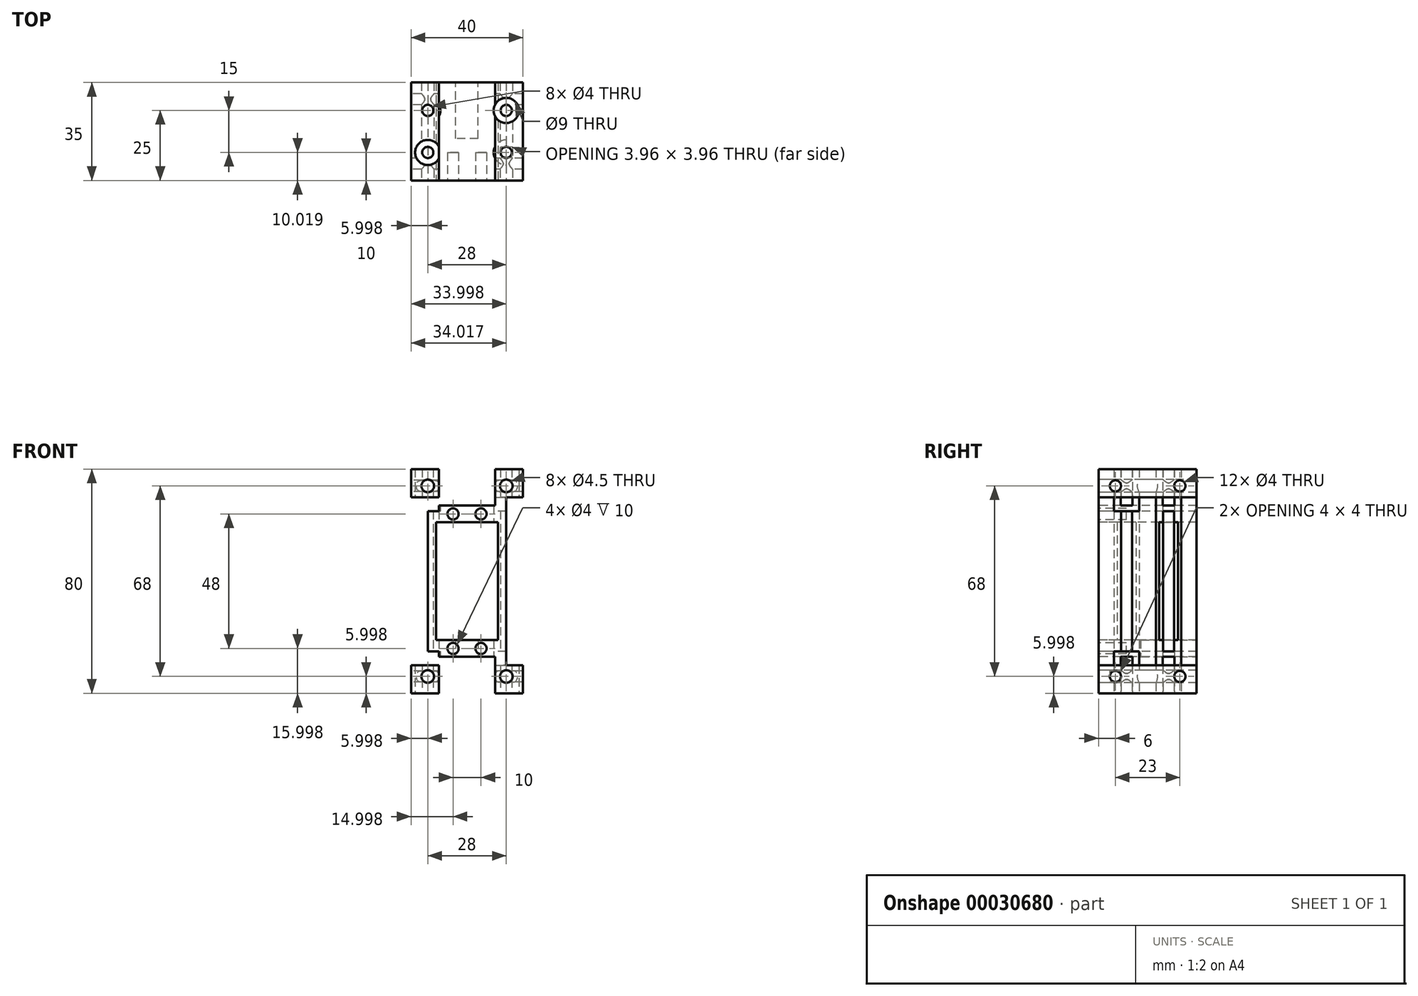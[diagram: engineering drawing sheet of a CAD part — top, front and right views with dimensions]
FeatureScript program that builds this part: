
annotation { "Feature Type Name" : "Feature", "Feature Type Description" : "" }
export const myFeature = defineFeature(function(context is Context, id is Id, definition is map)
    precondition{}
    {
        {
            var Q0;
            Q0=qCreatedBy(makeId("Front.planeOp"),FACE);
            var sketch = newSketch(context, id + "F0", { "sketchPlane" : qUnion([Q0])});
            skLineSegment(sketch, "E0.bottom", {"start": v(-33.97, 64.46) * mm, "end": v(6.03, 64.46) * mm});
            skLineSegment(sketch, "E0.top", {"start": v(-33.97, -15.54) * mm, "end": v(6.03, -15.54) * mm});
            skLineSegment(sketch, "E0.left", {"start": v(-33.97, 64.46) * mm, "end": v(-33.97, -15.54) * mm});
            skLineSegment(sketch, "E0.right", {"start": v(6.03, 64.46) * mm, "end": v(6.03, -15.54) * mm});
            skSolve(sketch);
        }
        {
            var Q0;
            Q0 = qSketchRegion(id + "F0", true);
            var Q1;
            Q1=makeQuery(id+"F0.imprint","IMPRINT",FACE,{"disambiguationData":[TD([[makeQuery(id+"F0.imprint","IMPRINT",EDGE,{"derivedFrom":sQuery(id+"F0.wireOp",EDGE,"E0.bottom")}),-1.0]])]});
            extrude(context, id + "F1", {"entities" : qUnion([Q0, Q1]), "depth" : 35 * mm});
        }
        {
            var Q0;
            Q0=makeQuery(id+"F1.opExtrude","CAP_FACE",FACE,{"disambiguationData":[OSD([sQuery(id+"F0.wireOp",EDGE,"E0.bottom"),sQuery(id+"F0.wireOp",EDGE,"E0.top"),sQuery(id+"F0.wireOp",EDGE,"E0.left"),sQuery(id+"F0.wireOp",EDGE,"E0.right")])],"isStart":false});
            var sketch = newSketch(context, id + "F2", { "sketchPlane" : qUnion([Q0])});
            skLineSegment(sketch, "E1.bottom", {"start": v(-24.97, 45.46) * mm, "end": v(-2.97, 45.46) * mm});
            skLineSegment(sketch, "E1.top", {"start": v(-24.97, 3.46) * mm, "end": v(-2.97, 3.46) * mm});
            skLineSegment(sketch, "E1.left", {"start": v(-24.97, 45.46) * mm, "end": v(-24.97, 3.46) * mm});
            skLineSegment(sketch, "E1.right", {"start": v(-2.97, 45.46) * mm, "end": v(-2.97, 3.46) * mm});
            skLineSegment(sketch, "E2", {"start": v(-13.97, 3.46) * mm, "end": v(-13.97, 13.46) * mm, "construction": true});
            skLineSegment(sketch, "E3.bottom", {"start": v(6.03, 54.46) * mm, "end": v(0.03, 54.46) * mm});
            skLineSegment(sketch, "E3.top", {"start": v(6.03, -5.54) * mm, "end": v(0.03, -5.54) * mm});
            skLineSegment(sketch, "E3.left", {"start": v(6.03, 54.46) * mm, "end": v(6.03, -5.54) * mm});
            skLineSegment(sketch, "E3.right", {"start": v(0.03, 54.46) * mm, "end": v(0.03, -5.54) * mm});
            skLineSegment(sketch, "E4", {"start": v(6.03, -5.54) * mm, "end": v(6.03, -15.54) * mm, "construction": true});
            skLineSegment(sketch, "E5", {"start": v(6.03, 54.46) * mm, "end": v(6.03, 64.46) * mm, "construction": true});
            skLineSegment(sketch, "E6.MirrorCS", {"start": v(-27.97, 54.46) * mm, "end": v(-27.97, -5.54) * mm});
            skLineSegment(sketch, "E7.MirrorCS", {"start": v(-33.97, 54.46) * mm, "end": v(-27.97, 54.46) * mm});
            skLineSegment(sketch, "E8.MirrorCS", {"start": v(-33.97, 54.46) * mm, "end": v(-33.97, -5.54) * mm});
            skLineSegment(sketch, "E9.MirrorCS", {"start": v(-33.97, -5.54) * mm, "end": v(-27.97, -5.54) * mm});
            skPoint(sketch, "E10", {"position": v(-33.97, 24.46) * mm});
            skLineSegment(sketch, "E11", {"start": v(-33.97, 24.46) * mm, "end": v(6.03, 24.46) * mm, "construction": true});
            skLineSegment(sketch, "E12.bottom", {"start": v(-3.97, -15.54) * mm, "end": v(-23.97, -15.54) * mm});
            skLineSegment(sketch, "E12.top", {"start": v(-3.97, -2.54) * mm, "end": v(-23.97, -2.54) * mm});
            skLineSegment(sketch, "E12.left", {"start": v(-3.97, -15.54) * mm, "end": v(-3.97, -2.54) * mm});
            skLineSegment(sketch, "E12.right", {"start": v(-23.97, -15.54) * mm, "end": v(-23.97, -2.54) * mm});
            skLineSegment(sketch, "E13", {"start": v(-3.97, -2.54) * mm, "end": v(0.03, -2.54) * mm, "construction": true});
            skLineSegment(sketch, "E14", {"start": v(-23.97, -2.54) * mm, "end": v(-27.97, -2.54) * mm, "construction": true});
            skLineSegment(sketch, "E15.MirrorCS", {"start": v(-23.97, 64.46) * mm, "end": v(-23.97, 51.46) * mm});
            skLineSegment(sketch, "E16.MirrorCS", {"start": v(-3.97, 51.46) * mm, "end": v(-23.97, 51.46) * mm});
            skLineSegment(sketch, "E17.MirrorCS", {"start": v(-3.97, 64.46) * mm, "end": v(-3.97, 51.46) * mm});
            skLineSegment(sketch, "E18.MirrorCS", {"start": v(-3.97, 64.46) * mm, "end": v(-23.97, 64.46) * mm});
            skSolve(sketch);
        }
        {
            var Q0;
            Q0 = qSketchRegion(id + "F2", true);
            extrude(context, id + "F3", {"entities" : qUnion([Q0]), "operationType" : NewBodyOperationType.REMOVE, "endBound" : BoundingType.THROUGH_ALL, "oppositeDirection" : true, "depth" : 35 * mm});
        }
        {
            var Q0;
            Q0=makeQuery(id+"F1.opExtrude","CAP_FACE",FACE,{"disambiguationData":[OSD([sQuery(id+"F0.wireOp",EDGE,"E0.bottom"),sQuery(id+"F0.wireOp",EDGE,"E0.top"),sQuery(id+"F0.wireOp",EDGE,"E0.left"),sQuery(id+"F0.wireOp",EDGE,"E0.right")])],"isStart":true});
            var sketch = newSketch(context, id + "F4", { "sketchPlane" : qUnion([Q0])});
            skLineSegment(sketch, "E19.bottom", {"start": v(9.97, 3.46) * mm, "end": v(17.97, 3.46) * mm});
            skLineSegment(sketch, "E19.top", {"start": v(9.97, -6.54) * mm, "end": v(17.97, -6.54) * mm});
            skLineSegment(sketch, "E19.left", {"start": v(9.97, 3.46) * mm, "end": v(9.97, -6.54) * mm});
            skLineSegment(sketch, "E19.right", {"start": v(17.97, 3.46) * mm, "end": v(17.97, -6.54) * mm});
            skSolve(sketch);
        }
        {
            var Q0;
            Q0 = qSketchRegion(id + "F4", true);
            extrude(context, id + "F5", {"entities" : qUnion([Q0]), "operationType" : NewBodyOperationType.REMOVE, "oppositeDirection" : true, "depth" : 20 * mm});
        }
        {
            var Q0;
            Q0=makeQuery(id+"F2.imprint","IMPRINT",FACE,{"disambiguationData":[TD([[makeQuery(id+"F2.imprint","IMPRINT",EDGE,{"derivedFrom":sQuery(id+"F2.wireOp",EDGE,"E1.bottom")}),1.0]])]});
            var sketch = newSketch(context, id + "F6", { "sketchPlane" : qUnion([Q0])});
            skCircle(sketch, "E20", {"center": v(-18.97, 48.46) * mm, "radius": 2 * mm});
            skCircle(sketch, "E21", {"center": v(-8.97, 48.46) * mm, "radius": 2 * mm});
            skCircle(sketch, "E22.MirrorC", {"center": v(-18.97, 0.46) * mm, "radius": 2 * mm});
            skCircle(sketch, "E23.MirrorC", {"center": v(-8.97, 0.46) * mm, "radius": 2 * mm});
            skPoint(sketch, "E24.orphan", {"position": v(-33.97, 54.46) * mm});
            skPoint(sketch, "E25.start.orphan", {"position": v(6.03, 59.46) * mm});
            skPoint(sketch, "E26.0.end.orphan", {"position": v(-33.97, 59.46) * mm});
            skPoint(sketch, "E26.0.start.orphan", {"position": v(-33.97, 64.46) * mm});
            skPoint(sketch, "E27.orphan", {"position": v(6.03, 54.46) * mm});
            skPoint(sketch, "E28.0.start.orphan", {"position": v(6.03, 64.46) * mm});
            skSolve(sketch);
        }
        {
            var Q0;
            Q0 = qSketchRegion(id + "F6", true);
            extrude(context, id + "F7", {"entities" : qUnion([Q0]), "operationType" : NewBodyOperationType.REMOVE, "oppositeDirection" : true, "depth" : 10 * mm});
        }
        {
            var Q0;
            Q0=makeQuery(id+"F2.imprint","IMPRINT",FACE,{"disambiguationData":[TD([[makeQuery(id+"F2.imprint","IMPRINT",EDGE,{"derivedFrom":sQuery(id+"F2.wireOp",EDGE,"E1.bottom")}),1.0]])]});
            var sketch = newSketch(context, id + "F8", { "sketchPlane" : qUnion([Q0])});
            skCircle(sketch, "E29", {"center": v(-27.97, 58.46) * mm, "radius": 2.25 * mm});
            skPoint(sketch, "E30.endSnap0", {"position": v(-8.97, 59.46) * mm});
            skPoint(sketch, "E30.end.orphan", {"position": v(-56.56, 59.46) * mm});
            skPoint(sketch, "E31.orphan", {"position": v(-23.97, 64.46) * mm});
            skPoint(sketch, "E32.0.end.orphan", {"position": v(6.03, 54.46) * mm});
            skPoint(sketch, "E33.0.end.orphan", {"position": v(-28.97, 64.46) * mm});
            skPoint(sketch, "E33.0.start.orphan", {"position": v(-33.97, 64.46) * mm});
            skCircle(sketch, "E34.MirrorC", {"center": v(-27.97, -9.54) * mm, "radius": 2.25 * mm});
            skCircle(sketch, "E35.MirrorC", {"center": v(0.03, 58.46) * mm, "radius": 2.25 * mm});
            skCircle(sketch, "E36.MirrorC", {"center": v(0.03, -9.54) * mm, "radius": 2.25 * mm});
            skSolve(sketch);
        }
        {
            var Q0;
            Q0 = qSketchRegion(id + "F8", true);
            extrude(context, id + "F9", {"entities" : qUnion([Q0]), "operationType" : NewBodyOperationType.REMOVE, "endBound" : BoundingType.THROUGH_ALL, "oppositeDirection" : true, "depth" : 25 * mm});
        }
        {
            var Q0;
            Q0=makeQuery(id+"F1.opExtrude","SWEPT_FACE",FACE,{"disambiguationData":[OSD([sQuery(id+"F0.wireOp",EDGE,"E0.left")])]});
            var sketch = newSketch(context, id + "F10", { "sketchPlane" : qUnion([Q0])});
            skCircle(sketch, "E37", {"center": v(6, 58.46) * mm, "radius": 2 * mm});
            skLineSegment(sketch, "E38", {"start": v(17.5, 64.46) * mm, "end": v(17.5, -15.54) * mm, "construction": true});
            skLineSegment(sketch, "E39", {"start": v(31.43, 24.46) * mm, "end": v(-3.57, 24.46) * mm, "construction": true});
            skCircle(sketch, "E40.MirrorC", {"center": v(6, -9.54) * mm, "radius": 2 * mm});
            skCircle(sketch, "E41.MirrorC", {"center": v(29, 58.46) * mm, "radius": 2 * mm});
            skCircle(sketch, "E42.MirrorC", {"center": v(29, -9.54) * mm, "radius": 2 * mm});
            skPoint(sketch, "E43", {"position": v(17.5, 24.46) * mm});
            skSolve(sketch);
        }
        {
            var Q0;
            Q0 = qSketchRegion(id + "F10", true);
            extrude(context, id + "F11", {"entities" : qUnion([Q0]), "operationType" : NewBodyOperationType.REMOVE, "endBound" : BoundingType.THROUGH_ALL, "oppositeDirection" : true, "depth" : 25 * mm});
        }
        {
            var Q0;
            Q0=makeQuery(id+"F1.opExtrude","SWEPT_FACE",FACE,{"disambiguationData":[OSD([sQuery(id+"F0.wireOp",EDGE,"E0.top")])]});
            var sketch = newSketch(context, id + "F12", { "sketchPlane" : qUnion([Q0])});
            skCircle(sketch, "E44", {"center": v(-27.97, 10) * mm, "radius": 2 * mm});
            skLineSegment(sketch, "E45.0", {"start": v(6.03, 0) * mm, "end": v(-33.97, 0) * mm, "construction": true});
            skLineSegment(sketch, "E46.0.0", {"start": v(-2.97, 35) * mm, "end": v(-24.97, 35) * mm});
            skLineSegment(sketch, "E46.0.2", {"start": v(-24.97, 35) * mm, "end": v(-2.97, 35) * mm});
            skPoint(sketch, "E47.0", {"position": v(6.03, 0) * mm});
            skLineSegment(sketch, "E48", {"start": v(-13.97, 0) * mm, "end": v(-13.97, 35) * mm, "construction": true});
            skLineSegment(sketch, "E49", {"start": v(-13.97, 17.5) * mm, "end": v(-20.38, 17.5) * mm, "construction": true});
            skCircle(sketch, "E50", {"center": v(-27.97, 10) * mm, "radius": 4.5 * mm});
            skCircle(sketch, "E51.MirrorC", {"center": v(-27.97, 25) * mm, "radius": 2 * mm});
            skCircle(sketch, "E52.MirrorC", {"center": v(-27.97, 25) * mm, "radius": 4.5 * mm});
            skCircle(sketch, "E53.MirrorC", {"center": v(0.03, 10) * mm, "radius": 2 * mm});
            skCircle(sketch, "E54.MirrorC", {"center": v(0.03, 10) * mm, "radius": 4.5 * mm});
            skCircle(sketch, "E55.MirrorC", {"center": v(0.03, 25) * mm, "radius": 2 * mm});
            skCircle(sketch, "E56.MirrorC", {"center": v(0.03, 25) * mm, "radius": 4.5 * mm});
            skSolve(sketch);
        }
        {
            var Q0;
            Q0=makeQuery(id+"F12.imprint","IMPRINT",FACE,{"disambiguationData":[TD([[makeQuery(id+"F12.imprint","IMPRINT",EDGE,{"derivedFrom":sQuery(id+"F12.wireOp",EDGE,"E44")}),1.0]])]});
            var Q1;
            Q1=makeQuery(id+"F12.imprint","IMPRINT",FACE,{"disambiguationData":[TD([[makeQuery(id+"F12.imprint","IMPRINT",EDGE,{"derivedFrom":sQuery(id+"F12.wireOp",EDGE,"E51.MirrorC")}),-1.0]])]});
            var Q2;
            Q2=makeQuery(id+"F12.imprint","IMPRINT",FACE,{"disambiguationData":[TD([[makeQuery(id+"F12.imprint","IMPRINT",EDGE,{"derivedFrom":sQuery(id+"F12.wireOp",EDGE,"E55.MirrorC")}),1.0]])]});
            var Q3;
            Q3=makeQuery(id+"F12.imprint","IMPRINT",FACE,{"disambiguationData":[TD([[makeQuery(id+"F12.imprint","IMPRINT",EDGE,{"derivedFrom":sQuery(id+"F12.wireOp",EDGE,"E53.MirrorC")}),-1.0]])]});
            var Q4;
            Q4=makeQuery(id+"F1.opExtrude","SWEPT_FACE",FACE,{"disambiguationData":[OSD([sQuery(id+"F0.wireOp",EDGE,"E0.bottom")])]});
            extrude(context, id + "F13", {"entities" : qUnion([Q0, Q1, Q2, Q3]), "operationType" : NewBodyOperationType.REMOVE, "endBound" : BoundingType.UP_TO_SURFACE, "oppositeDirection" : true, "endBoundEntityFace" : qUnion([Q4]), "depth" : 25 * mm});
        }
        {
            var Q0;
            Q0=makeQuery(id+"F12.imprint","IMPRINT",FACE,{"disambiguationData":[TD([[makeQuery(id+"F12.imprint","IMPRINT",EDGE,{"derivedFrom":sQuery(id+"F12.wireOp",EDGE,"E44")}),-1.0]])]});
            var Q1;
            Q1=makeQuery(id+"F12.imprint","IMPRINT",FACE,{"disambiguationData":[TD([[makeQuery(id+"F12.imprint","IMPRINT",EDGE,{"derivedFrom":sQuery(id+"F12.wireOp",EDGE,"E51.MirrorC")}),1.0]])]});
            var Q2;
            Q2=makeQuery(id+"F12.imprint","IMPRINT",FACE,{"disambiguationData":[TD([[makeQuery(id+"F12.imprint","IMPRINT",EDGE,{"derivedFrom":sQuery(id+"F12.wireOp",EDGE,"E55.MirrorC")}),-1.0]])]});
            var Q3;
            Q3=makeQuery(id+"F12.imprint","IMPRINT",FACE,{"disambiguationData":[TD([[makeQuery(id+"F12.imprint","IMPRINT",EDGE,{"derivedFrom":sQuery(id+"F12.wireOp",EDGE,"E53.MirrorC")}),1.0]])]});
            var Q4;
            {var subQ0=sQuery(id+"F12.wireOp",EDGE,"E52.MirrorC");var subQ1=makeQuery(id+"F3.boolean.opBoolean","COPY",EDGE,{"derivedFrom":makeQuery(id+"F3.opExtrude","SWEPT_EDGE",EDGE,{"disambiguationData":[OSD([sQuery(id+"F0.wireOp",EDGE,"E0.top"),sQuery(id+"F2.wireOp",EDGE,"E12.bottom"),sQuery(id+"F2.wireOp",EDGE,"E12.right")])]})});var subQ2=makeQuery(id+"F12.imprint","INTERSECT",VERTEX,{"disambiguationData":[OD(0.0)],"derivedFrom":[subQ1,subQ0]});Q4=makeQuery(id+"F12.imprint","IMPRINT",FACE,{"disambiguationData":[TD([[makeQuery(id+"F12.imprint","IMPRINT",EDGE,{"disambiguationData":[TD([[subQ2,-1.0]])],"derivedFrom":subQ0}),-1.0]])]});}
            var Q5;
            {var subQ0=sQuery(id+"F12.wireOp",EDGE,"E56.MirrorC");var subQ1=makeQuery(id+"F3.boolean.opBoolean","COPY",EDGE,{"derivedFrom":makeQuery(id+"F3.opExtrude","SWEPT_EDGE",EDGE,{"disambiguationData":[OSD([sQuery(id+"F0.wireOp",EDGE,"E0.top"),sQuery(id+"F2.wireOp",EDGE,"E12.bottom"),sQuery(id+"F2.wireOp",EDGE,"E12.left")])]})});var subQ2=makeQuery(id+"F12.imprint","INTERSECT",VERTEX,{"disambiguationData":[OD(0.0)],"derivedFrom":[subQ1,subQ0]});Q5=makeQuery(id+"F12.imprint","IMPRINT",FACE,{"disambiguationData":[TD([[makeQuery(id+"F12.imprint","IMPRINT",EDGE,{"disambiguationData":[TD([[subQ2,-1.0]])],"derivedFrom":subQ0}),1.0]])]});}
            var Q6;
            {var subQ0=sQuery(id+"F12.wireOp",EDGE,"E54.MirrorC");var subQ1=makeQuery(id+"F3.boolean.opBoolean","COPY",EDGE,{"derivedFrom":makeQuery(id+"F3.opExtrude","SWEPT_EDGE",EDGE,{"disambiguationData":[OSD([sQuery(id+"F0.wireOp",EDGE,"E0.top"),sQuery(id+"F2.wireOp",EDGE,"E12.bottom"),sQuery(id+"F2.wireOp",EDGE,"E12.left")])]})});var subQ2=makeQuery(id+"F12.imprint","INTERSECT",VERTEX,{"disambiguationData":[OD(0.0)],"derivedFrom":[subQ1,subQ0]});Q6=makeQuery(id+"F12.imprint","IMPRINT",FACE,{"disambiguationData":[TD([[makeQuery(id+"F12.imprint","IMPRINT",EDGE,{"disambiguationData":[TD([[subQ2,-1.0]])],"derivedFrom":subQ0}),-1.0]])]});}
            var Q7;
            {var subQ0=sQuery(id+"F12.wireOp",EDGE,"E50");var subQ1=makeQuery(id+"F3.boolean.opBoolean","COPY",EDGE,{"derivedFrom":makeQuery(id+"F3.opExtrude","SWEPT_EDGE",EDGE,{"disambiguationData":[OSD([sQuery(id+"F0.wireOp",EDGE,"E0.top"),sQuery(id+"F2.wireOp",EDGE,"E12.bottom"),sQuery(id+"F2.wireOp",EDGE,"E12.right")])]})});var subQ2=makeQuery(id+"F12.imprint","INTERSECT",VERTEX,{"disambiguationData":[OD(0.0)],"derivedFrom":[subQ1,subQ0]});Q7=makeQuery(id+"F12.imprint","IMPRINT",FACE,{"disambiguationData":[TD([[makeQuery(id+"F12.imprint","IMPRINT",EDGE,{"disambiguationData":[TD([[subQ2,-1.0]])],"derivedFrom":subQ0}),1.0]])]});}
            extrude(context, id + "F14", {"entities" : qUnion([Q0, Q1, Q2, Q3, Q4, Q5, Q6, Q7]), "operationType" : NewBodyOperationType.REMOVE, "oppositeDirection" : true, "depth" : 15 * mm, "hasSecondDirection" : true, "secondDirectionOppositeDirection" : true, "secondDirectionDepth" : 10 * mm});
        }
        {
            var Q0;
            Q0=makeQuery(id+"F12.imprint","IMPRINT",FACE,{"disambiguationData":[TD([[makeQuery(id+"F12.imprint","IMPRINT",EDGE,{"derivedFrom":sQuery(id+"F12.wireOp",EDGE,"E51.MirrorC")}),1.0]])]});
            var Q1;
            Q1=makeQuery(id+"F12.imprint","IMPRINT",FACE,{"disambiguationData":[TD([[makeQuery(id+"F12.imprint","IMPRINT",EDGE,{"derivedFrom":sQuery(id+"F12.wireOp",EDGE,"E44")}),-1.0]])]});
            var Q2;
            {var subQ0=sQuery(id+"F12.wireOp",EDGE,"E52.MirrorC");var subQ1=makeQuery(id+"F3.boolean.opBoolean","COPY",EDGE,{"derivedFrom":makeQuery(id+"F3.opExtrude","SWEPT_EDGE",EDGE,{"disambiguationData":[OSD([sQuery(id+"F0.wireOp",EDGE,"E0.top"),sQuery(id+"F2.wireOp",EDGE,"E12.bottom"),sQuery(id+"F2.wireOp",EDGE,"E12.right")])]})});var subQ2=makeQuery(id+"F12.imprint","INTERSECT",VERTEX,{"disambiguationData":[OD(0.0)],"derivedFrom":[subQ1,subQ0]});Q2=makeQuery(id+"F12.imprint","IMPRINT",FACE,{"disambiguationData":[TD([[makeQuery(id+"F12.imprint","IMPRINT",EDGE,{"disambiguationData":[TD([[subQ2,-1.0]])],"derivedFrom":subQ0}),-1.0]])]});}
            var Q3;
            {var subQ0=sQuery(id+"F12.wireOp",EDGE,"E50");var subQ1=makeQuery(id+"F3.boolean.opBoolean","COPY",EDGE,{"derivedFrom":makeQuery(id+"F3.opExtrude","SWEPT_EDGE",EDGE,{"disambiguationData":[OSD([sQuery(id+"F0.wireOp",EDGE,"E0.top"),sQuery(id+"F2.wireOp",EDGE,"E12.bottom"),sQuery(id+"F2.wireOp",EDGE,"E12.right")])]})});var subQ2=makeQuery(id+"F12.imprint","INTERSECT",VERTEX,{"disambiguationData":[OD(0.0)],"derivedFrom":[subQ1,subQ0]});Q3=makeQuery(id+"F12.imprint","IMPRINT",FACE,{"disambiguationData":[TD([[makeQuery(id+"F12.imprint","IMPRINT",EDGE,{"disambiguationData":[TD([[subQ2,-1.0]])],"derivedFrom":subQ0}),1.0]])]});}
            var Q4;
            Q4=makeQuery(id+"F12.imprint","IMPRINT",FACE,{"disambiguationData":[TD([[makeQuery(id+"F12.imprint","IMPRINT",EDGE,{"derivedFrom":sQuery(id+"F12.wireOp",EDGE,"E55.MirrorC")}),-1.0]])]});
            var Q5;
            {var subQ0=sQuery(id+"F12.wireOp",EDGE,"E56.MirrorC");var subQ1=makeQuery(id+"F3.boolean.opBoolean","COPY",EDGE,{"derivedFrom":makeQuery(id+"F3.opExtrude","SWEPT_EDGE",EDGE,{"disambiguationData":[OSD([sQuery(id+"F0.wireOp",EDGE,"E0.top"),sQuery(id+"F2.wireOp",EDGE,"E12.bottom"),sQuery(id+"F2.wireOp",EDGE,"E12.left")])]})});var subQ2=makeQuery(id+"F12.imprint","INTERSECT",VERTEX,{"disambiguationData":[OD(0.0)],"derivedFrom":[subQ1,subQ0]});Q5=makeQuery(id+"F12.imprint","IMPRINT",FACE,{"disambiguationData":[TD([[makeQuery(id+"F12.imprint","IMPRINT",EDGE,{"disambiguationData":[TD([[subQ2,-1.0]])],"derivedFrom":subQ0}),1.0]])]});}
            var Q6;
            Q6=makeQuery(id+"F12.imprint","IMPRINT",FACE,{"disambiguationData":[TD([[makeQuery(id+"F12.imprint","IMPRINT",EDGE,{"derivedFrom":sQuery(id+"F12.wireOp",EDGE,"E53.MirrorC")}),1.0]])]});
            var Q7;
            {var subQ0=sQuery(id+"F12.wireOp",EDGE,"E54.MirrorC");var subQ1=makeQuery(id+"F3.boolean.opBoolean","COPY",EDGE,{"derivedFrom":makeQuery(id+"F3.opExtrude","SWEPT_EDGE",EDGE,{"disambiguationData":[OSD([sQuery(id+"F0.wireOp",EDGE,"E0.top"),sQuery(id+"F2.wireOp",EDGE,"E12.bottom"),sQuery(id+"F2.wireOp",EDGE,"E12.left")])]})});var subQ2=makeQuery(id+"F12.imprint","INTERSECT",VERTEX,{"disambiguationData":[OD(0.0)],"derivedFrom":[subQ1,subQ0]});Q7=makeQuery(id+"F12.imprint","IMPRINT",FACE,{"disambiguationData":[TD([[makeQuery(id+"F12.imprint","IMPRINT",EDGE,{"disambiguationData":[TD([[subQ2,-1.0]])],"derivedFrom":subQ0}),-1.0]])]});}
            var Q8;
            Q8=makeQuery(id+"F3.boolean.opBoolean","COPY",FACE,{"derivedFrom":makeQuery(id+"F3.opExtrude","SWEPT_FACE",FACE,{"disambiguationData":[OSD([sQuery(id+"F2.wireOp",EDGE,"E7.MirrorCS")])]})});
            var Q9;
            Q9=makeQuery(id+"F14.boolean.opBoolean","MERGE",FACE,{"derivedFrom":[makeQuery(id+"F3.boolean.opBoolean","COPY",FACE,{"derivedFrom":makeQuery(id+"F3.opExtrude","SWEPT_FACE",FACE,{"disambiguationData":[OSD([sQuery(id+"F2.wireOp",EDGE,"E9.MirrorCS")])]})}),makeQuery(id+"F14.opExtrude","CAP_FACE",FACE,{"disambiguationData":[OSD([sQuery(id+"F12.wireOp",EDGE,"E44"),sQuery(id+"F12.wireOp",EDGE,"E50")])],"isStart":true}),makeQuery(id+"F14.opExtrude","CAP_FACE",FACE,{"disambiguationData":[OSD([sQuery(id+"F12.wireOp",EDGE,"E51.MirrorC"),sQuery(id+"F12.wireOp",EDGE,"E52.MirrorC")])],"isStart":true})]});
            extrude(context, id + "F15", {"entities" : qUnion([Q0, Q1, Q2, Q3, Q4, Q5, Q6, Q7]), "operationType" : NewBodyOperationType.REMOVE, "endBound" : BoundingType.UP_TO_SURFACE, "oppositeDirection" : true, "endBoundEntityFace" : qUnion([Q8]), "depth" : 25 * mm, "hasSecondDirection" : true, "secondDirectionOppositeDirection" : true, "secondDirectionBoundEntityFace" : qUnion([Q9]), "secondDirectionDepth" : 65 * mm});
        }
    });
